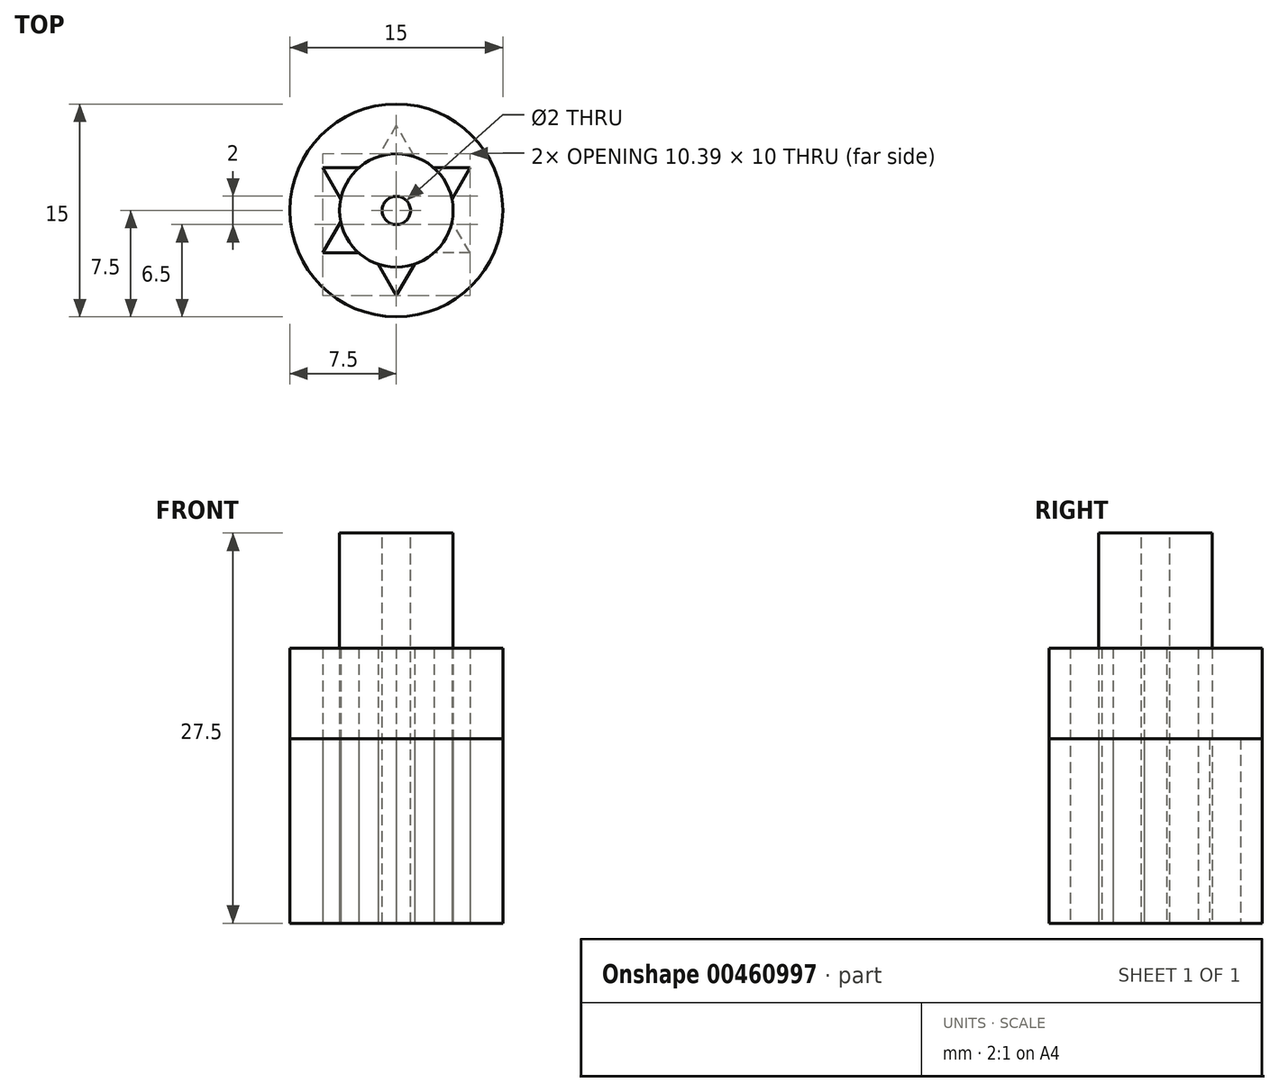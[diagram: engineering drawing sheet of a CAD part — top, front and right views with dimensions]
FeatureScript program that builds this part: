
annotation { "Feature Type Name" : "Feature", "Feature Type Description" : "" }
export const myFeature = defineFeature(function(context is Context, id is Id, definition is map)
    precondition{}
    {
        {
            var Q0;
            Q0=qCreatedBy(makeId("Top.planeOp"),FACE);
            var sketch = newSketch(context, id + "F0", { "sketchPlane" : qUnion([Q0])});
            skCircle(sketch, "E0", {"center": v(0, 0) * mm, "radius": 7.5 * mm});
            skCircle(sketch, "E1", {"center": v(0, 0) * mm, "radius": 4 * mm});
            skCircle(sketch, "E2", {"center": v(0, 0) * mm, "radius": 6 * mm, "construction": true});
            skPoint(sketch, "E3", {"position": v(0, 6) * mm});
            skPoint(sketch, "E4.1.0", {"position": v(5.2, 3) * mm});
            skPoint(sketch, "E4.2.0", {"position": v(5.2, -3) * mm});
            skPoint(sketch, "E4.3.0", {"position": v(0, -6) * mm});
            skPoint(sketch, "E4.4.0", {"position": v(-5.2, -3) * mm});
            skPoint(sketch, "E4.5.0", {"position": v(-5.2, 3) * mm});
            skLineSegment(sketch, "E5", {"start": v(0, 6) * mm, "end": v(-5.2, -3) * mm});
            skLineSegment(sketch, "E6", {"start": v(5.2, 3) * mm, "end": v(-5.2, 3) * mm});
            skLineSegment(sketch, "E7", {"start": v(-5.2, 3) * mm, "end": v(0, -6) * mm});
            skLineSegment(sketch, "E8", {"start": v(0, -6) * mm, "end": v(5.2, 3) * mm});
            skLineSegment(sketch, "E9", {"start": v(5.2, -3) * mm, "end": v(0, 6) * mm});
            skLineSegment(sketch, "E10", {"start": v(5.2, -3) * mm, "end": v(-5.2, -3) * mm});
            skSolve(sketch);
        }
        {
            var Q0;
            {var subQ0=sQuery(id+"F0.wireOp",EDGE,"E10");var subQ1=sQuery(id+"F0.wireOp",EDGE,"E1");var subQ2=makeQuery(id+"F0.imprint","INTERSECT",VERTEX,{"disambiguationData":[OD(1.0)],"derivedFrom":[subQ1,subQ0]});Q0=makeQuery(id+"F0.imprint","IMPRINT",FACE,{"disambiguationData":[TD([[makeQuery(id+"F0.imprint","IMPRINT",EDGE,{"disambiguationData":[TD([[subQ2,-1.0]])],"derivedFrom":subQ1}),-1.0]])]});}
            var Q1;
            {var subQ0=sQuery(id+"F0.wireOp",EDGE,"E5");var subQ1=sQuery(id+"F0.wireOp",EDGE,"E1");var subQ2=makeQuery(id+"F0.imprint","INTERSECT",VERTEX,{"disambiguationData":[OD(1.0)],"derivedFrom":[subQ1,subQ0]});Q1=makeQuery(id+"F0.imprint","IMPRINT",FACE,{"disambiguationData":[TD([[makeQuery(id+"F0.imprint","IMPRINT",EDGE,{"disambiguationData":[TD([[subQ2,-1.0]])],"derivedFrom":subQ1}),-1.0]])]});}
            var Q2;
            {var subQ0=sQuery(id+"F0.wireOp",EDGE,"E9");var subQ1=sQuery(id+"F0.wireOp",EDGE,"E1");var subQ2=makeQuery(id+"F0.imprint","INTERSECT",VERTEX,{"disambiguationData":[OD(0.0)],"derivedFrom":[subQ1,subQ0]});Q2=makeQuery(id+"F0.imprint","IMPRINT",FACE,{"disambiguationData":[TD([[makeQuery(id+"F0.imprint","IMPRINT",EDGE,{"disambiguationData":[TD([[subQ2,-1.0]])],"derivedFrom":subQ1}),-1.0]])]});}
            extrude(context, id + "F1", {"entities" : qUnion([Q0, Q1, Q2]), "depth" : 19.4 * mm});
        }
        {
            var Q0;
            {var subQ0=sQuery(id+"F0.wireOp",EDGE,"E6");var subQ1=sQuery(id+"F0.wireOp",EDGE,"E1");var subQ2=makeQuery(id+"F0.imprint","INTERSECT",VERTEX,{"disambiguationData":[OD(1.0)],"derivedFrom":[subQ1,subQ0]});Q0=makeQuery(id+"F0.imprint","IMPRINT",FACE,{"disambiguationData":[TD([[makeQuery(id+"F0.imprint","IMPRINT",EDGE,{"disambiguationData":[TD([[subQ2,-1.0]])],"derivedFrom":subQ1}),1.0]])]});}
            var Q1;
            {var subQ0=sQuery(id+"F0.wireOp",EDGE,"E5");var subQ1=sQuery(id+"F0.wireOp",EDGE,"E1");var subQ2=makeQuery(id+"F0.imprint","INTERSECT",VERTEX,{"disambiguationData":[OD(0.0)],"derivedFrom":[subQ1,subQ0]});Q1=makeQuery(id+"F0.imprint","IMPRINT",FACE,{"disambiguationData":[TD([[makeQuery(id+"F0.imprint","IMPRINT",EDGE,{"disambiguationData":[TD([[subQ2,-1.0]])],"derivedFrom":subQ1}),1.0]])]});}
            var Q2;
            {var subQ0=sQuery(id+"F0.wireOp",EDGE,"E9");var subQ1=sQuery(id+"F0.wireOp",EDGE,"E1");var subQ2=makeQuery(id+"F0.imprint","INTERSECT",VERTEX,{"disambiguationData":[OD(0.0)],"derivedFrom":[subQ1,subQ0]});Q2=makeQuery(id+"F0.imprint","IMPRINT",FACE,{"disambiguationData":[TD([[makeQuery(id+"F0.imprint","IMPRINT",EDGE,{"disambiguationData":[TD([[subQ2,-1.0]])],"derivedFrom":subQ1}),1.0]])]});}
            var Q3;
            {var subQ0=sQuery(id+"F0.wireOp",EDGE,"E6");var subQ1=sQuery(id+"F0.wireOp",EDGE,"E1");var subQ2=makeQuery(id+"F0.imprint","INTERSECT",VERTEX,{"disambiguationData":[OD(0.0)],"derivedFrom":[subQ1,subQ0]});Q3=makeQuery(id+"F0.imprint","IMPRINT",FACE,{"disambiguationData":[TD([[makeQuery(id+"F0.imprint","IMPRINT",EDGE,{"disambiguationData":[TD([[subQ2,-1.0]])],"derivedFrom":subQ1}),1.0]])]});}
            var Q4;
            {var subQ0=sQuery(id+"F0.wireOp",EDGE,"E6");var subQ1=sQuery(id+"F0.wireOp",EDGE,"E1");var subQ2=makeQuery(id+"F0.imprint","INTERSECT",VERTEX,{"disambiguationData":[OD(0.0)],"derivedFrom":[subQ1,subQ0]});Q4=makeQuery(id+"F0.imprint","IMPRINT",FACE,{"disambiguationData":[TD([[makeQuery(id+"F0.imprint","IMPRINT",EDGE,{"disambiguationData":[TD([[subQ2,1.0]])],"derivedFrom":subQ1}),1.0]])]});}
            var Q5;
            {var subQ0=sQuery(id+"F0.wireOp",EDGE,"E8");var subQ1=sQuery(id+"F0.wireOp",EDGE,"E1");var subQ2=makeQuery(id+"F0.imprint","INTERSECT",VERTEX,{"disambiguationData":[OD(0.0)],"derivedFrom":[subQ1,subQ0]});Q5=makeQuery(id+"F0.imprint","IMPRINT",FACE,{"disambiguationData":[TD([[makeQuery(id+"F0.imprint","IMPRINT",EDGE,{"disambiguationData":[TD([[subQ2,1.0]])],"derivedFrom":subQ1}),1.0]])]});}
            var Q6;
            {var subQ0=sQuery(id+"F0.wireOp",EDGE,"E10");var subQ1=sQuery(id+"F0.wireOp",EDGE,"E1");var subQ2=makeQuery(id+"F0.imprint","INTERSECT",VERTEX,{"disambiguationData":[OD(1.0)],"derivedFrom":[subQ1,subQ0]});Q6=makeQuery(id+"F0.imprint","IMPRINT",FACE,{"disambiguationData":[TD([[makeQuery(id+"F0.imprint","IMPRINT",EDGE,{"disambiguationData":[TD([[subQ2,-1.0]])],"derivedFrom":subQ1}),1.0]])]});}
            var Q7;
            {var subQ0=sQuery(id+"F0.wireOp",EDGE,"E7");var subQ1=sQuery(id+"F0.wireOp",EDGE,"E1");var subQ2=makeQuery(id+"F0.imprint","INTERSECT",VERTEX,{"disambiguationData":[OD(1.0)],"derivedFrom":[subQ1,subQ0]});Q7=makeQuery(id+"F0.imprint","IMPRINT",FACE,{"disambiguationData":[TD([[makeQuery(id+"F0.imprint","IMPRINT",EDGE,{"disambiguationData":[TD([[subQ2,-1.0]])],"derivedFrom":subQ1}),1.0]])]});}
            var Q8;
            {var subQ0=sQuery(id+"F0.wireOp",EDGE,"E10");var subQ1=sQuery(id+"F0.wireOp",EDGE,"E1");var subQ2=makeQuery(id+"F0.imprint","INTERSECT",VERTEX,{"disambiguationData":[OD(0.0)],"derivedFrom":[subQ1,subQ0]});Q8=makeQuery(id+"F0.imprint","IMPRINT",FACE,{"disambiguationData":[TD([[makeQuery(id+"F0.imprint","IMPRINT",EDGE,{"disambiguationData":[TD([[subQ2,-1.0]])],"derivedFrom":subQ1}),1.0]])]});}
            var Q9;
            {var subQ0=sQuery(id+"F0.wireOp",EDGE,"E5");var subQ1=sQuery(id+"F0.wireOp",EDGE,"E1");var subQ2=makeQuery(id+"F0.imprint","INTERSECT",VERTEX,{"disambiguationData":[OD(1.0)],"derivedFrom":[subQ1,subQ0]});Q9=makeQuery(id+"F0.imprint","IMPRINT",FACE,{"disambiguationData":[TD([[makeQuery(id+"F0.imprint","IMPRINT",EDGE,{"disambiguationData":[TD([[subQ2,-1.0]])],"derivedFrom":subQ1}),1.0]])]});}
            var Q10;
            {var subQ0=sQuery(id+"F0.wireOp",EDGE,"E7");var subQ1=sQuery(id+"F0.wireOp",EDGE,"E1");var subQ2=makeQuery(id+"F0.imprint","INTERSECT",VERTEX,{"disambiguationData":[OD(0.0)],"derivedFrom":[subQ1,subQ0]});Q10=makeQuery(id+"F0.imprint","IMPRINT",FACE,{"disambiguationData":[TD([[makeQuery(id+"F0.imprint","IMPRINT",EDGE,{"disambiguationData":[TD([[subQ2,-1.0]])],"derivedFrom":subQ1}),1.0]])]});}
            var Q11;
            {var subQ6=sQuery(id+"F0.wireOp",EDGE,"E5");var subQ9=sQuery(id+"F0.wireOp",EDGE,"E6");var subQ10=makeQuery(id+"F0.imprint","INTERSECT",VERTEX,{"derivedFrom":[subQ6,subQ9]});Q11=makeQuery(id+"F0.imprint","IMPRINT",FACE,{"disambiguationData":[TD([[makeQuery(id+"F0.imprint","IMPRINT",EDGE,{"disambiguationData":[TD([[subQ10,-1.0]])],"derivedFrom":subQ6}),1.0]])]});}
            var Q12;
            {var subQ0=sQuery(id+"F0.wireOp",EDGE,"E8");var subQ1=sQuery(id+"F0.wireOp",EDGE,"E1");var subQ2=makeQuery(id+"F0.imprint","INTERSECT",VERTEX,{"disambiguationData":[OD(1.0)],"derivedFrom":[subQ1,subQ0]});Q12=makeQuery(id+"F0.imprint","IMPRINT",FACE,{"disambiguationData":[TD([[makeQuery(id+"F0.imprint","IMPRINT",EDGE,{"disambiguationData":[TD([[subQ2,-1.0]])],"derivedFrom":subQ1}),1.0]])]});}
            extrude(context, id + "F2", {"entities" : qUnion([Q0, Q1, Q2, Q3, Q4, Q5, Q6, Q7, Q8, Q9, Q10, Q11, Q12]), "depth" : 27.5 * mm});
        }
        {
            var Q0;
            Q0=makeQuery(id+"F0.imprint","IMPRINT",FACE,{"disambiguationData":[TD([[makeQuery(id+"F0.imprint","IMPRINT",EDGE,{"derivedFrom":sQuery(id+"F0.wireOp",EDGE,"E0")}),1.0]])]});
            var Q1;
            {var subQ0=sQuery(id+"F0.wireOp",EDGE,"E6");var subQ1=sQuery(id+"F0.wireOp",EDGE,"E1");var subQ2=makeQuery(id+"F0.imprint","INTERSECT",VERTEX,{"disambiguationData":[OD(1.0)],"derivedFrom":[subQ1,subQ0]});Q1=makeQuery(id+"F0.imprint","IMPRINT",FACE,{"disambiguationData":[TD([[makeQuery(id+"F0.imprint","IMPRINT",EDGE,{"disambiguationData":[TD([[subQ2,-1.0]])],"derivedFrom":subQ1}),-1.0]])]});}
            var Q2;
            {var subQ0=sQuery(id+"F0.wireOp",EDGE,"E6");var subQ1=sQuery(id+"F0.wireOp",EDGE,"E1");var subQ2=makeQuery(id+"F0.imprint","INTERSECT",VERTEX,{"disambiguationData":[OD(0.0)],"derivedFrom":[subQ1,subQ0]});Q2=makeQuery(id+"F0.imprint","IMPRINT",FACE,{"disambiguationData":[TD([[makeQuery(id+"F0.imprint","IMPRINT",EDGE,{"disambiguationData":[TD([[subQ2,1.0]])],"derivedFrom":subQ1}),-1.0]])]});}
            var Q3;
            {var subQ0=sQuery(id+"F0.wireOp",EDGE,"E7");var subQ1=sQuery(id+"F0.wireOp",EDGE,"E1");var subQ2=makeQuery(id+"F0.imprint","INTERSECT",VERTEX,{"disambiguationData":[OD(1.0)],"derivedFrom":[subQ1,subQ0]});Q3=makeQuery(id+"F0.imprint","IMPRINT",FACE,{"disambiguationData":[TD([[makeQuery(id+"F0.imprint","IMPRINT",EDGE,{"disambiguationData":[TD([[subQ2,-1.0]])],"derivedFrom":subQ1}),-1.0]])]});}
            extrude(context, id + "F3", {"entities" : qUnion([Q0, Q1, Q2, Q3]), "depth" : 13 * mm});
        }
        {
            var Q0;
            Q0=makeQuery(id+"F2.opExtrude","CAP_FACE",FACE,{"disambiguationData":[OSD([sQuery(id+"F0.wireOp",EDGE,"E1")])],"isStart":false});
            var sketch = newSketch(context, id + "F4", { "sketchPlane" : qUnion([Q0])});
            skCircle(sketch, "E11", {"center": v(0, 0) * mm, "radius": 1 * mm});
            skSolve(sketch);
        }
        {
            var Q0;
            Q0=makeQuery(id+"F4.imprint","IMPRINT",FACE,{"disambiguationData":[TD([[makeQuery(id+"F4.imprint","IMPRINT",EDGE,{"derivedFrom":sQuery(id+"F4.wireOp",EDGE,"E11")}),1.0]])]});
            extrude(context, id + "F5", {"entities" : qUnion([Q0]), "operationType" : NewBodyOperationType.REMOVE, "oppositeDirection" : true, "depth" : 30 * mm});
        }
    });
